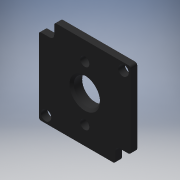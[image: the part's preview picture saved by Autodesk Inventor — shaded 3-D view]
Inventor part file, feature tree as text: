
AUTODESK INVENTOR PART (.ipt)
format: ipt  version: 2016 (Build 200138000, 138)  size: 264,192 bytes
history: native  units: in
note: dims shown in document units (in); Inventor stores cm internally (conversion verified against a paired STEP export)
features: fillet x1
ambient origin geometry x8: Origin, YZ Plane, XZ Plane, XY Plane, X Axis, Y Axis, Z Axis, Center Point
bodies: Solid1 (feature_tree)
feature tree (1):
  fillet  "Fillet4"  [1 undecoded]
note: 1 required parameter value undecoded (feature->parameter linkage not recoverable at this tier; creation-order binding heuristic only, values carry confidence <= 0.55)
